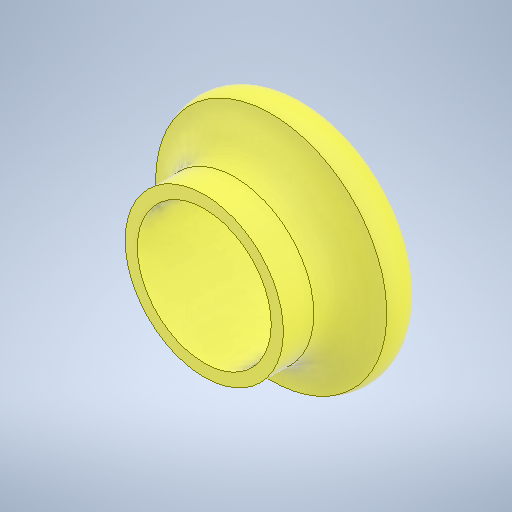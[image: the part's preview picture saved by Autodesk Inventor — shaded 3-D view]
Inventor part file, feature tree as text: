
AUTODESK INVENTOR PART (.ipt)
format: ipt  version: 2025.1 (Build 291241000, 241)  size: 311,296 bytes
history: native  units: mm
features: sketch x2, revolve x1, hole x1
ambient origin geometry x8: Origin, YZ Plane, XZ Plane, XY Plane, X Axis, Y Axis, Z Axis, Center Point
bodies: Solid1 (feature_tree)
feature tree (4):
  revolve  "Revolution1"  [1 undecoded]
  hole  "Hole1"  [1 undecoded]
  sketch  "Sketch1"  dims[d0=4.0mm d1=6.0mm]
  sketch  "Sketch2"  dims[d2=38.0mm d3=11.0mm d4=26.0mm d5=90.0deg d6=22.0mm d7=6.0mm d8=4.0mm d9=2.0mm d10=90.0deg d11=8.0mm d12=0.0mm d13=6.0mm]
note: 2 required parameter values undecoded (feature->parameter linkage not recoverable at this tier; creation-order binding heuristic only, values carry confidence <= 0.55)